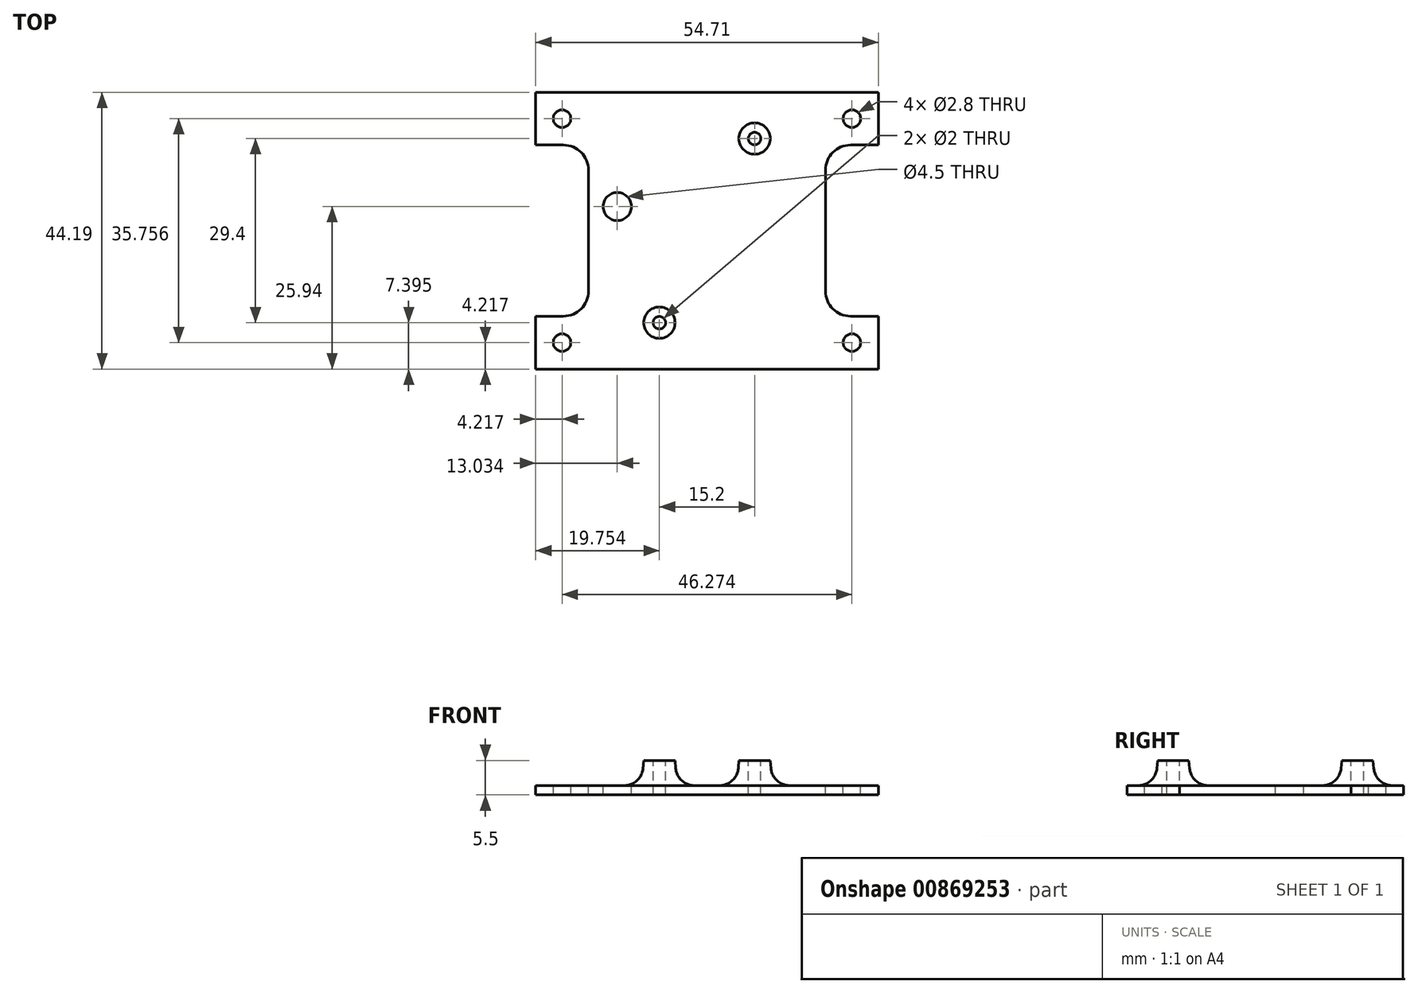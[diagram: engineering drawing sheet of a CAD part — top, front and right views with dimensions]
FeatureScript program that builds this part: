
annotation { "Feature Type Name" : "Feature", "Feature Type Description" : "" }
export const myFeature = defineFeature(function(context is Context, id is Id, definition is map)
    precondition{}
    {
        {
            var Q0;
            Q0=qCreatedBy(makeId("Top.planeOp"),FACE);
            var sketch = newSketch(context, id + "F0", { "sketchPlane" : qUnion([Q0])});
            skLineSegment(sketch, "E0.bottom", {"start": v(0, 0) * mm, "end": v(51.3, 0) * mm});
            skLineSegment(sketch, "E0.top", {"start": v(0, 74) * mm, "end": v(51.3, 74) * mm});
            skLineSegment(sketch, "E0.left", {"start": v(0, 0) * mm, "end": v(0, 74) * mm});
            skLineSegment(sketch, "E0.right", {"start": v(51.3, 0) * mm, "end": v(51.3, 74) * mm});
            skLineSegment(sketch, "E1.bottom", {"start": v(0, 69) * mm, "end": v(16.7, 69) * mm, "construction": true});
            skLineSegment(sketch, "E1.top", {"start": v(0, 55) * mm, "end": v(16.7, 55) * mm, "construction": true});
            skLineSegment(sketch, "E1.left", {"start": v(0, 69) * mm, "end": v(0, 55) * mm, "construction": true});
            skLineSegment(sketch, "E1.right", {"start": v(16.7, 69) * mm, "end": v(16.7, 55) * mm, "construction": true});
            skLineSegment(sketch, "E2.bottom", {"start": v(0, 33) * mm, "end": v(16.7, 33) * mm, "construction": true});
            skLineSegment(sketch, "E2.top", {"start": v(0, 19) * mm, "end": v(16.7, 19) * mm, "construction": true});
            skLineSegment(sketch, "E2.left", {"start": v(0, 33) * mm, "end": v(0, 19) * mm, "construction": true});
            skLineSegment(sketch, "E2.right", {"start": v(16.7, 33) * mm, "end": v(16.7, 19) * mm, "construction": true});
            skLineSegment(sketch, "E3.bottom", {"start": v(51.3, 69) * mm, "end": v(34.6, 69) * mm, "construction": true});
            skLineSegment(sketch, "E3.top", {"start": v(51.3, 55) * mm, "end": v(34.6, 55) * mm, "construction": true});
            skLineSegment(sketch, "E3.left", {"start": v(51.3, 69) * mm, "end": v(51.3, 55) * mm, "construction": true});
            skLineSegment(sketch, "E3.right", {"start": v(34.6, 69) * mm, "end": v(34.6, 55) * mm, "construction": true});
            skLineSegment(sketch, "E4.bottom", {"start": v(51.3, 33) * mm, "end": v(34.6, 33) * mm, "construction": true});
            skLineSegment(sketch, "E4.top", {"start": v(51.3, 19) * mm, "end": v(34.6, 19) * mm, "construction": true});
            skLineSegment(sketch, "E4.left", {"start": v(51.3, 33) * mm, "end": v(51.3, 19) * mm, "construction": true});
            skLineSegment(sketch, "E4.right", {"start": v(34.6, 33) * mm, "end": v(34.6, 19) * mm, "construction": true});
            skCircle(sketch, "E5", {"center": v(11.21, 3.92) * mm, "radius": 1.6 * mm});
            skCircle(sketch, "E6", {"center": v(32.51, 3.92) * mm, "radius": 1.6 * mm});
            skCircle(sketch, "E7", {"center": v(49.43, 3.92) * mm, "radius": 1.6 * mm});
            skCircle(sketch, "E8", {"center": v(49.43, 72.12) * mm, "radius": 1.6 * mm});
            skCircle(sketch, "E9", {"center": v(1.88, 72.12) * mm, "radius": 1.6 * mm});
            skLineSegment(sketch, "E10", {"start": v(1.88, 72.12) * mm, "end": v(49.43, 72.12) * mm, "construction": true});
            skSolve(sketch);
        }
        {
            var Q0;
            {var subQ10=sQuery(id+"F0.wireOp",EDGE,"E0.bottom");Q0=makeQuery(id+"F0.imprint","IMPRINT",FACE,{"disambiguationData":[TD([[makeQuery(id+"F0.imprint","IMPRINT",EDGE,{"derivedFrom":subQ10}),1.0]])]});}
            var sketch = newSketch(context, id + "F1", { "sketchPlane" : qUnion([Q0])});
            skLineSegment(sketch, "E11.0", {"start": v(-1.7, -1.7) * mm, "end": v(-1.7, 75.7) * mm});
            skLineSegment(sketch, "E11.1", {"start": v(-1.7, -1.7) * mm, "end": v(53, -1.7) * mm});
            skLineSegment(sketch, "E11.2", {"start": v(53, -1.7) * mm, "end": v(53, 75.7) * mm});
            skLineSegment(sketch, "E11.3", {"start": v(-1.7, 75.7) * mm, "end": v(53, 75.7) * mm});
            skSolve(sketch);
        }
        {
            var Q0;
            Q0=qSketchRegion(id+"F1",true);
            extrude(context, id + "F2", {"entities" : qUnion([Q0]), "depth" : 1.5 * mm, "offsetDistance" : 25 * mm});
        }
        {
            var Q0;
            {var subQ0=sQuery(id+"F6GXzuOHntquvKr_1.wireOp",EDGE,"s17BW498-6bKE-bvLq-Xut5-QpTvFKj44F6L");var subQ1=sQuery(id+"F6GXzuOHntquvKr_1.wireOp",EDGE,"KkH5eE3K-AXJX-ZvZF-UOav-HisGAflkKzs7");var subQ2=sQuery(id+"F6GXzuOHntquvKr_1.wireOp",EDGE,"Lc9ymual-iNm1-0gbj-nJ7k-jOShu6Us2LTm");var subQ3=sQuery(id+"F6GXzuOHntquvKr_1.wireOp",EDGE,"rWmqq6mH-Y7ee-QEVy-FZAS-sSJdcVXWXRMh");var subQ4=sQuery(id+"F6GXzuOHntquvKr_1.wireOp",EDGE,"c878682a-a3fc-495e-9975-6ad3af1e72822.MirrorCS");var subQ5=sQuery(id+"F6GXzuOHntquvKr_1.wireOp",EDGE,"c878682a-a3fc-495e-9975-6ad3af1e72821.MirrorCS");var subQ6=sQuery(id+"F6GXzuOHntquvKr_1.wireOp",EDGE,"c878682a-a3fc-495e-9975-6ad3af1e72820.MirrorCS");var subQ7=sQuery(id+"F6GXzuOHntquvKr_1.wireOp",EDGE,"gumsQsr6-K8Im-hkzl-JbXD-zjOCVHvVJb9f");var subQ8=sQuery(id+"F6GXzuOHntquvKr_1.wireOp",EDGE,"ybwg6MaK-QAga-Fhxh-U395-XssyxfBwCAxj");var subQ9=sQuery(id+"F6GXzuOHntquvKr_1.wireOp",EDGE,"c878682a-a3fc-495e-9975-6ad3af1e72826.MirrorCS");var subQ10=sQuery(id+"F1.wireOp",EDGE,"E11.1");var subQ11=sQuery(id+"F6GXzuOHntquvKr_1.wireOp",EDGE,"JJFlnewm-85mE-duSD-FSQs-iFHrIXV6r2m2");var subQ12=sQuery(id+"F1.wireOp",EDGE,"E11.3");var subQ13=sQuery(id+"F6GXzuOHntquvKr_1.wireOp",EDGE,"c878682a-a3fc-495e-9975-6ad3af1e72823.MirrorCS");var subQ14=sQuery(id+"F1.wireOp",EDGE,"E11.0");var subQ15=sQuery(id+"F6GXzuOHntquvKr_1.wireOp",EDGE,"c878682a-a3fc-495e-9975-6ad3af1e72827.MirrorCS");var subQ16=sQuery(id+"F1.wireOp",EDGE,"E11.2");var subQ17=sQuery(id+"F6GXzuOHntquvKr_1.wireOp",EDGE,"KYmkqSoi-ySKa-ysJT-3wLy-sUcAUlMoE4Lw");var subQ18=sQuery(id+"F6GXzuOHntquvKr_1.wireOp",EDGE,"rGfCT0qz-87yu-6z5P-5utD-09FTJLvzhlS5");var subQ19=sQuery(id+"F6GXzuOHntquvKr_1.wireOp",EDGE,"38AYfzUa-mGmV-3WPU-EBOK-ykPB0kyNFQ41");Q0=makeQuery(id+"F7ymWyKb8andwvf_1.boolean.opBoolean","SPLIT",FACE,{"disambiguationData":[TD([makeQuery(id+"F2.opExtrude","SWEPT_FACE",FACE,{"disambiguationData":[OSD([subQ14])]})])],"derivedFrom":makeQuery(id+"F7FFp2r9aQODMAd_1.boolean.opBoolean","MERGE",FACE,{"derivedFrom":[makeQuery(id+"F2.opExtrude","CAP_FACE",FACE,{"disambiguationData":[OSD([subQ14,subQ10,subQ16,subQ12])],"isStart":false}),makeQuery(id+"F7FFp2r9aQODMAd_1.opExtrude","CAP_FACE",FACE,{"disambiguationData":[OSD([subQ17,subQ1,subQ18,sQuery(id+"F6GXzuOHntquvKr_1.wireOp",EDGE,"2ph3kAtd-Sgn4-jQcT-vLBk-Z36Royi8zWen"),subQ11])],"isStart":false}),makeQuery(id+"F7FFp2r9aQODMAd_1.opExtrude","CAP_FACE",FACE,{"disambiguationData":[OSD([subQ8,subQ19,subQ0,sQuery(id+"F6GXzuOHntquvKr_1.wireOp",EDGE,"SVgNKyan-8M9S-muwL-MN39-nCX4EP7pWvKC"),subQ2])],"isStart":false}),makeQuery(id+"F7FFp2r9aQODMAd_1.opExtrude","CAP_FACE",FACE,{"disambiguationData":[OSD([subQ6,subQ4,sQuery(id+"F6GXzuOHntquvKr_1.wireOp",EDGE,"c878682a-a3fc-495e-9975-6ad3af1e72824.MirrorCS"),subQ15,subQ3])],"isStart":false}),makeQuery(id+"F7FFp2r9aQODMAd_1.opExtrude","CAP_FACE",FACE,{"disambiguationData":[OSD([subQ5,subQ13,sQuery(id+"F6GXzuOHntquvKr_1.wireOp",EDGE,"c878682a-a3fc-495e-9975-6ad3af1e72825.MirrorCS"),subQ9,subQ7])],"isStart":false})]})});}
            var sketch = newSketch(context, id + "F3", { "sketchPlane" : qUnion([Q0])});
            skLineSegment(sketch, "E12.bottom", {"start": v(6.73, 8.81) * mm, "end": v(44.57, 8.81) * mm, "construction": true});
            skLineSegment(sketch, "E12.top", {"start": v(6.73, 69) * mm, "end": v(44.57, 69) * mm, "construction": true});
            skLineSegment(sketch, "E12.left", {"start": v(6.73, 8.8) * mm, "end": v(6.73, 69) * mm, "construction": true});
            skLineSegment(sketch, "E12.right", {"start": v(44.57, 8.81) * mm, "end": v(44.57, 69) * mm, "construction": true});
            skLineSegment(sketch, "E13", {"start": v(6.73, 38.9) * mm, "end": v(44.57, 38.9) * mm, "construction": true});
            skLineSegment(sketch, "E14", {"start": v(25.65, 8.81) * mm, "end": v(25.65, 69) * mm, "construction": true});
            skLineSegment(sketch, "E15.bottom", {"start": v(6.73, 16.8) * mm, "end": v(-1.7, 16.8) * mm});
            skLineSegment(sketch, "E15.top", {"start": v(6.73, 25.24) * mm, "end": v(-1.7, 25.24) * mm});
            skLineSegment(sketch, "E16.MirrorCS", {"start": v(44.57, 25.24) * mm, "end": v(53, 25.24) * mm});
            skLineSegment(sketch, "E17.MirrorCS", {"start": v(44.57, 16.81) * mm, "end": v(53, 16.81) * mm});
            skLineSegment(sketch, "E18.MirrorCS", {"start": v(6.73, 61) * mm, "end": v(-1.7, 61) * mm});
            skLineSegment(sketch, "E19.MirrorCS", {"start": v(44.57, 61) * mm, "end": v(53, 61) * mm});
            skLineSegment(sketch, "E20.MirrorCS", {"start": v(44.57, 52.57) * mm, "end": v(53, 52.57) * mm});
            skLineSegment(sketch, "E21.MirrorCS", {"start": v(6.73, 52.57) * mm, "end": v(-1.7, 52.57) * mm});
            skCircle(sketch, "E22", {"center": v(2.52, 21.03) * mm, "radius": 1.4 * mm});
            skPoint(sketch, "E22.centerSnap1", {"position": v(-1.7, 21.03) * mm});
            skCircle(sketch, "E23.MirrorC", {"center": v(48.8, 21.03) * mm, "radius": 1.4 * mm});
            skCircle(sketch, "E24.MirrorC", {"center": v(48.8, 56.78) * mm, "radius": 1.4 * mm});
            skCircle(sketch, "E25.MirrorC", {"center": v(2.52, 56.78) * mm, "radius": 1.4 * mm});
            skLineSegment(sketch, "E26.bottom", {"start": v(15.55, 60.6) * mm, "end": v(35.75, 60.6) * mm, "construction": true});
            skLineSegment(sketch, "E26.top", {"start": v(15.55, 17.2) * mm, "end": v(35.75, 17.2) * mm, "construction": true});
            skLineSegment(sketch, "E26.left", {"start": v(15.55, 60.6) * mm, "end": v(15.55, 17.2) * mm, "construction": true});
            skLineSegment(sketch, "E26.right", {"start": v(35.75, 60.6) * mm, "end": v(35.75, 17.2) * mm, "construction": true});
            skLineSegment(sketch, "E27", {"start": v(2.52, 56.78) * mm, "end": v(48.8, 56.78) * mm, "construction": true});
            skLineSegment(sketch, "E28", {"start": v(48.8, 56.78) * mm, "end": v(48.8, 21.03) * mm, "construction": true});
            skLineSegment(sketch, "E29", {"start": v(48.8, 21.03) * mm, "end": v(2.52, 21.03) * mm, "construction": true});
            skLineSegment(sketch, "E30", {"start": v(2.52, 21.03) * mm, "end": v(2.52, 56.78) * mm, "construction": true});
            skLineSegment(sketch, "E31", {"start": v(6.73, 61) * mm, "end": v(44.57, 61) * mm});
            skLineSegment(sketch, "E32", {"start": v(6.73, 16.8) * mm, "end": v(44.57, 16.81) * mm});
            skLineSegment(sketch, "E33", {"start": v(6.73, 52.57) * mm, "end": v(6.73, 25.24) * mm});
            skLineSegment(sketch, "E34", {"start": v(44.57, 52.57) * mm, "end": v(44.57, 25.24) * mm});
            skLineSegment(sketch, "E35", {"start": v(-1.7, 61) * mm, "end": v(-1.7, 75.7) * mm});
            skLineSegment(sketch, "E36", {"start": v(-1.7, 75.7) * mm, "end": v(53, 75.7) * mm});
            skLineSegment(sketch, "E37", {"start": v(53, 75.7) * mm, "end": v(53, 61) * mm});
            skLineSegment(sketch, "E38", {"start": v(53, 52.57) * mm, "end": v(53, 25.24) * mm});
            skLineSegment(sketch, "E39", {"start": v(53, 16.81) * mm, "end": v(53, -1.7) * mm});
            skLineSegment(sketch, "E40", {"start": v(53, -1.7) * mm, "end": v(-1.7, -1.7) * mm});
            skLineSegment(sketch, "E41", {"start": v(-1.7, -1.7) * mm, "end": v(-1.7, 16.8) * mm});
            skLineSegment(sketch, "E42", {"start": v(-1.7, 25.24) * mm, "end": v(-1.7, 52.57) * mm});
            skCircle(sketch, "E43", {"center": v(33.25, 53.6) * mm, "radius": 1 * mm});
            skCircle(sketch, "E44", {"center": v(18.05, 24.2) * mm, "radius": 1 * mm});
            skLineSegment(sketch, "E45", {"start": v(15.55, 38.9) * mm, "end": v(35.75, 38.9) * mm, "construction": true});
            skLineSegment(sketch, "E46", {"start": v(25.65, 60.6) * mm, "end": v(25.65, 17.2) * mm, "construction": true});
            skCircle(sketch, "E47", {"center": v(11.33, 42.75) * mm, "radius": 2.25 * mm});
            skSolve(sketch);
        }
        {
            var Q0;
            Q0 = qSketchRegion(id + "F3", true);
            extrude(context, id + "F4", {"entities" : qUnion([Q0]), "operationType" : NewBodyOperationType.REMOVE, "endBound" : BoundingType.THROUGH_ALL, "oppositeDirection" : true, "depth" : 25 * mm, "offsetDistance" : 25 * mm});
        }
        {
            var Q0;
            Q0=makeQuery(id+"F4.boolean.opBoolean","COPY",EDGE,{"derivedFrom":makeQuery(id+"F4.opExtrude","SWEPT_EDGE",EDGE,{"disambiguationData":[OSD([sQuery(id+"F1.wireOp",EDGE,"E11.0"),sQuery(id+"F3.wireOp",EDGE,"E18.MirrorCS"),sQuery(id+"F3.wireOp",EDGE,"E35")])]})});
            var Q1;
            Q1=makeQuery(id+"F4.boolean.opBoolean","COPY",EDGE,{"derivedFrom":makeQuery(id+"F4.opExtrude","SWEPT_EDGE",EDGE,{"disambiguationData":[OSD([sQuery(id+"F1.wireOp",EDGE,"E11.0"),sQuery(id+"F3.wireOp",EDGE,"E21.MirrorCS"),sQuery(id+"F3.wireOp",EDGE,"E42")])]})});
            var Q2;
            Q2=makeQuery(id+"F4.boolean.opBoolean","COPY",EDGE,{"derivedFrom":makeQuery(id+"F4.opExtrude","SWEPT_EDGE",EDGE,{"disambiguationData":[OSD([sQuery(id+"F1.wireOp",EDGE,"E11.0"),sQuery(id+"F3.wireOp",EDGE,"E15.top"),sQuery(id+"F3.wireOp",EDGE,"E42")])]})});
            var Q3;
            Q3=makeQuery(id+"F4.boolean.opBoolean","COPY",EDGE,{"derivedFrom":makeQuery(id+"F4.opExtrude","SWEPT_EDGE",EDGE,{"disambiguationData":[OSD([sQuery(id+"F1.wireOp",EDGE,"E11.0"),sQuery(id+"F3.wireOp",EDGE,"E15.bottom"),sQuery(id+"F3.wireOp",EDGE,"E41")])]})});
            var Q4;
            Q4=makeQuery(id+"F4.boolean.opBoolean","COPY",EDGE,{"derivedFrom":makeQuery(id+"F4.opExtrude","SWEPT_EDGE",EDGE,{"disambiguationData":[OSD([sQuery(id+"F3.wireOp",EDGE,"E15.top"),sQuery(id+"F3.wireOp",EDGE,"E33")])]})});
            var Q5;
            Q5=makeQuery(id+"F4.boolean.opBoolean","COPY",EDGE,{"derivedFrom":makeQuery(id+"F4.opExtrude","SWEPT_EDGE",EDGE,{"disambiguationData":[OSD([sQuery(id+"F3.wireOp",EDGE,"E21.MirrorCS"),sQuery(id+"F3.wireOp",EDGE,"E33")])]})});
            var Q6;
            Q6=makeQuery(id+"F4.boolean.opBoolean","COPY",EDGE,{"derivedFrom":makeQuery(id+"F4.opExtrude","SWEPT_EDGE",EDGE,{"disambiguationData":[OSD([sQuery(id+"F1.wireOp",EDGE,"E11.2"),sQuery(id+"F3.wireOp",EDGE,"E19.MirrorCS"),sQuery(id+"F3.wireOp",EDGE,"E37")])]})});
            var Q7;
            Q7=makeQuery(id+"F4.boolean.opBoolean","COPY",EDGE,{"derivedFrom":makeQuery(id+"F4.opExtrude","SWEPT_EDGE",EDGE,{"disambiguationData":[OSD([sQuery(id+"F1.wireOp",EDGE,"E11.2"),sQuery(id+"F3.wireOp",EDGE,"E20.MirrorCS"),sQuery(id+"F3.wireOp",EDGE,"E38")])]})});
            var Q8;
            Q8=makeQuery(id+"F4.boolean.opBoolean","COPY",EDGE,{"derivedFrom":makeQuery(id+"F4.opExtrude","SWEPT_EDGE",EDGE,{"disambiguationData":[OSD([sQuery(id+"F3.wireOp",EDGE,"E20.MirrorCS"),sQuery(id+"F3.wireOp",EDGE,"E34")])]})});
            var Q9;
            Q9=makeQuery(id+"F4.boolean.opBoolean","COPY",EDGE,{"derivedFrom":makeQuery(id+"F4.opExtrude","SWEPT_EDGE",EDGE,{"disambiguationData":[OSD([sQuery(id+"F3.wireOp",EDGE,"E16.MirrorCS"),sQuery(id+"F3.wireOp",EDGE,"E34")])]})});
            var Q10;
            Q10=makeQuery(id+"F4.boolean.opBoolean","COPY",EDGE,{"derivedFrom":makeQuery(id+"F4.opExtrude","SWEPT_EDGE",EDGE,{"disambiguationData":[OSD([sQuery(id+"F1.wireOp",EDGE,"E11.2"),sQuery(id+"F3.wireOp",EDGE,"E16.MirrorCS"),sQuery(id+"F3.wireOp",EDGE,"E38")])]})});
            var Q11;
            Q11=makeQuery(id+"F4.boolean.opBoolean","COPY",EDGE,{"derivedFrom":makeQuery(id+"F4.opExtrude","SWEPT_EDGE",EDGE,{"disambiguationData":[OSD([sQuery(id+"F1.wireOp",EDGE,"E11.2"),sQuery(id+"F3.wireOp",EDGE,"E17.MirrorCS"),sQuery(id+"F3.wireOp",EDGE,"E39")])]})});
            fillet(context, id + "F5", {"entities" : qUnion([Q0, Q1, Q2, Q3, Q4, Q5, Q6, Q7, Q8, Q9, Q10, Q11]), "radius" : 4 * mm, "tangentPropagation" : true, "allowEdgeOverflow" : false});
        }
        {
            var Q0;
            Q0=makeQuery(id+"F2.opExtrude","CAP_FACE",FACE,{"disambiguationData":[OSD([sQuery(id+"F1.wireOp",EDGE,"E11.0"),sQuery(id+"F1.wireOp",EDGE,"E11.1"),sQuery(id+"F1.wireOp",EDGE,"E11.2"),sQuery(id+"F1.wireOp",EDGE,"E11.3")])],"isStart":false});
            var sketch = newSketch(context, id + "F6", { "sketchPlane" : qUnion([Q0])});
            skCircle(sketch, "E48", {"center": v(18.05, 24.2) * mm, "radius": 3 * mm});
            skCircle(sketch, "E49", {"center": v(33.25, 53.6) * mm, "radius": 3 * mm});
            skCircle(sketch, "E50", {"center": v(18.05, 24.2) * mm, "radius": 1 * mm});
            skCircle(sketch, "E51", {"center": v(33.25, 53.6) * mm, "radius": 1 * mm});
            skSolve(sketch);
        }
        {
            var Q0;
            Q0 = qSketchRegion(id + "F6", true);
            extrude(context, id + "F7", {"entities" : qUnion([Q0]), "operationType" : NewBodyOperationType.ADD, "depth" : 4 * mm, "offsetDistance" : 25 * mm});
        }
        {
            var Q0;
            Q0=makeQuery(id+"F7.opExtrude","CAP_EDGE",EDGE,{"disambiguationData":[OSD([sQuery(id+"F6.wireOp",EDGE,"E48")])],"isStart":false});
            var Q1;
            Q1=makeQuery(id+"F7.opExtrude","CAP_EDGE",EDGE,{"disambiguationData":[OSD([sQuery(id+"F6.wireOp",EDGE,"E49")])],"isStart":false});
            chamfer(context, id + "F8", {"entities" : qUnion([Q0, Q1]), "chamferType" : ChamferType.OFFSET_ANGLE, "width" : .5 * mm, "oppositeDirection" : false, "angle" : 85 * degree, "tangentPropagation" : true});
        }
        {
            var Q0;
            Q0=makeQuery(id+"F8.opChamfer","BLEND_EDGE",EDGE,{"blendedFrom":[makeQuery(id+"F7.opExtrude","CAP_EDGE",EDGE,{"disambiguationData":[OSD([sQuery(id+"F6.wireOp",EDGE,"E48")])],"isStart":false}),makeQuery(id+"F2.opExtrude","CAP_FACE",FACE,{"disambiguationData":[OSD([sQuery(id+"F1.wireOp",EDGE,"E11.0"),sQuery(id+"F1.wireOp",EDGE,"E11.1"),sQuery(id+"F1.wireOp",EDGE,"E11.2"),sQuery(id+"F1.wireOp",EDGE,"E11.3")])],"isStart":false})],"blendedInto":[makeQuery(id+"F2.opExtrude","CAP_FACE",FACE,{"disambiguationData":[OSD([sQuery(id+"F1.wireOp",EDGE,"E11.0"),sQuery(id+"F1.wireOp",EDGE,"E11.1"),sQuery(id+"F1.wireOp",EDGE,"E11.2"),sQuery(id+"F1.wireOp",EDGE,"E11.3")])],"isStart":false})]});
            var Q1;
            Q1=makeQuery(id+"F8.opChamfer","BLEND_EDGE",EDGE,{"blendedFrom":[makeQuery(id+"F7.opExtrude","CAP_EDGE",EDGE,{"disambiguationData":[OSD([sQuery(id+"F6.wireOp",EDGE,"E49")])],"isStart":false}),makeQuery(id+"F2.opExtrude","CAP_FACE",FACE,{"disambiguationData":[OSD([sQuery(id+"F1.wireOp",EDGE,"E11.0"),sQuery(id+"F1.wireOp",EDGE,"E11.1"),sQuery(id+"F1.wireOp",EDGE,"E11.2"),sQuery(id+"F1.wireOp",EDGE,"E11.3")])],"isStart":false})],"blendedInto":[makeQuery(id+"F2.opExtrude","CAP_FACE",FACE,{"disambiguationData":[OSD([sQuery(id+"F1.wireOp",EDGE,"E11.0"),sQuery(id+"F1.wireOp",EDGE,"E11.1"),sQuery(id+"F1.wireOp",EDGE,"E11.2"),sQuery(id+"F1.wireOp",EDGE,"E11.3")])],"isStart":false})]});
            fillet(context, id + "F9", {"entities" : qUnion([Q0, Q1]), "radius" : 3 * mm, "tangentPropagation" : true, "allowEdgeOverflow" : false});
        }
    });
